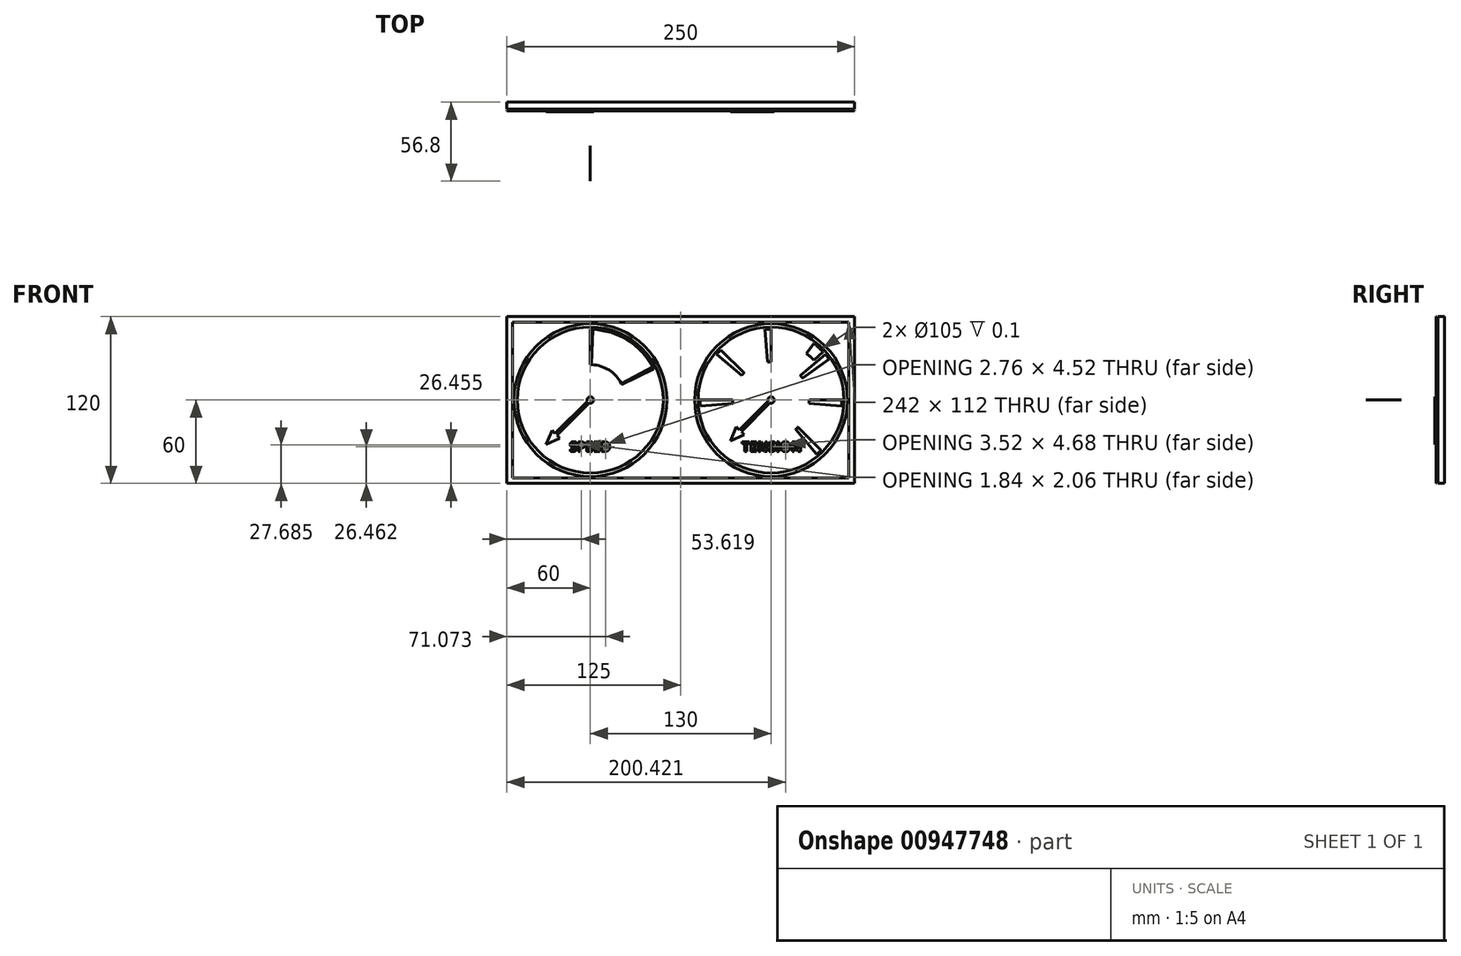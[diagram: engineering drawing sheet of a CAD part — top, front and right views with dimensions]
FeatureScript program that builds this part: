
annotation { "Feature Type Name" : "Feature", "Feature Type Description" : "" }
export const myFeature = defineFeature(function(context is Context, id is Id, definition is map)
    precondition{}
    {
        {
            var Q0;
            Q0=qCreatedBy(makeId("Right.planeOp"),FACE);
            var sketch = newSketch(context, id + "F0", { "sketchPlane" : qUnion([Q0])});
            skLineSegment(sketch, "E0", {"start": v(0, 0) * mm, "end": v(-116.06, 0) * mm, "construction": true});
            skSolve(sketch);
        }
        {
            var Q0;
            Q0=qCreatedBy(makeId("Right.planeOp"),FACE);
            var Q1;
            Q1=sQuery(id+"F0.wireOp",EDGE,"E0");
            cPlane(context, id + "F1", {"entities" : qUnion([Q0, Q1]), "cplaneType" : CPlaneType.LINE_ANGLE, "offset" : 25 * mm, "angle" : 135 * degree, "width" : 150 * mm, "height" : 150 * mm});
        }
        {
            var Q0;
            Q0=qCreatedBy(id+"F1.planeOp",FACE);
            var sketch = newSketch(context, id + "F2", { "sketchPlane" : qUnion([Q0])});
            skLineSegment(sketch, "E1.bottom", {"start": v(-25.4, 0) * mm, "end": v(-50.8, 0) * mm});
            skLineSegment(sketch, "E1.top", {"start": v(-25.4, 0) * mm, "end": v(-50.8, 0) * mm});
            skLineSegment(sketch, "E1.left", {"start": v(-25.4, 0) * mm, "end": v(-25.4, 0) * mm});
            skLineSegment(sketch, "E1.right", {"start": v(-50.8, 0) * mm, "end": v(-50.8, 0) * mm});
            skSolve(sketch);
        }
        {
            var Q0;
            Q0=qSketchRegion(id+"F2",true);
            var Q1;
            Q1=sQuery(id+"F0.wireOp",EDGE,"E0");
            revolve(context, id + "F3", {"surfaceOperationType" : NewSurfaceOperationType.NEW, "entities" : qUnion([Q0]), "axis" : qUnion([Q1]), "revolveType" : RevolveType.ONE_DIRECTION, "oppositeDirection" : true, "angle" : 135 * degree});
        }
        {
            var Q0;
            Q0=qCreatedBy(makeId("Right.planeOp"),FACE);
            var sketch = newSketch(context, id + "F4", { "sketchPlane" : qUnion([Q0])});
            skLineSegment(sketch, "E2.bottom", {"start": v(-0.01, 50.8) * mm, "end": v(0, 50.8) * mm});
            skLineSegment(sketch, "E2.top", {"start": v(0, 25.4) * mm, "end": v(0, 25.4) * mm});
            skLineSegment(sketch, "E2.left", {"start": v(-0.01, 50.8) * mm, "end": v(0, 25.4) * mm});
            skLineSegment(sketch, "E2.right", {"start": v(0, 50.8) * mm, "end": v(0, 25.4) * mm});
            skSolve(sketch);
        }
        {
            var Q0;
            Q0=qSketchRegion(id+"F4",true);
            var Q1;
            Q1=sQuery(id+"F0.wireOp",EDGE,"E0");
            revolve(context, id + "F5", {"surfaceOperationType" : NewSurfaceOperationType.NEW, "entities" : qUnion([Q0]), "axis" : qUnion([Q1]), "revolveType" : RevolveType.ONE_DIRECTION, "oppositeDirection" : true, "angle" : 2 * degree});
        }
        {
            var Q0;
            Q0=qCreatedBy(makeId("Right.planeOp"),FACE);
            var Q1;
            Q1=sQuery(id+"F0.wireOp",EDGE,"E0");
            cPlane(context, id + "F6", {"entities" : qUnion([Q0, Q1]), "cplaneType" : CPlaneType.LINE_ANGLE, "offset" : 25 * mm, "angle" : 2 * degree, "oppositeDirection" : true, "width" : 150 * mm, "height" : 150 * mm});
        }
        {
            var Q0;
            Q0=qCreatedBy(id+"F6.planeOp",FACE);
            var sketch = newSketch(context, id + "F7", { "sketchPlane" : qUnion([Q0])});
            skLineSegment(sketch, "E3.bottom", {"start": v(0, 50.8) * mm, "end": v(0, 50.8) * mm});
            skLineSegment(sketch, "E3.top", {"start": v(0, 25.4) * mm, "end": v(0, 25.4) * mm});
            skLineSegment(sketch, "E3.left", {"start": v(0, 50.8) * mm, "end": v(0, 25.4) * mm});
            skLineSegment(sketch, "E3.right", {"start": v(0, 50.8) * mm, "end": v(0, 25.4) * mm});
            skSolve(sketch);
        }
        {
            var Q0;
            Q0=qSketchRegion(id+"F7",true);
            var Q1;
            Q1=sQuery(id+"F0.wireOp",EDGE,"E0");
            revolve(context, id + "F8", {"surfaceOperationType" : NewSurfaceOperationType.NEW, "entities" : qUnion([Q0]), "axis" : qUnion([Q1]), "revolveType" : RevolveType.ONE_DIRECTION, "oppositeDirection" : true, "angle" : 60 * degree});
        }
        {
            var Q0;
            Q0=qCreatedBy(id+"F6.planeOp",FACE);
            var Q1;
            Q1=sQuery(id+"F0.wireOp",EDGE,"E0");
            cPlane(context, id + "F9", {"entities" : qUnion([Q0, Q1]), "cplaneType" : CPlaneType.LINE_ANGLE, "offset" : 25 * mm, "angle" : 60 * degree, "oppositeDirection" : true, "width" : 150 * mm, "height" : 150 * mm});
        }
        {
            var Q0;
            Q0=qCreatedBy(id+"F9.planeOp",FACE);
            var sketch = newSketch(context, id + "F10", { "sketchPlane" : qUnion([Q0])});
            skLineSegment(sketch, "E4.bottom", {"start": v(50.8, 0) * mm, "end": v(25.4, 0) * mm});
            skLineSegment(sketch, "E4.top", {"start": v(50.8, 0) * mm, "end": v(25.4, -0.01) * mm});
            skLineSegment(sketch, "E4.left", {"start": v(50.8, 0) * mm, "end": v(50.8, 0) * mm});
            skLineSegment(sketch, "E4.right", {"start": v(25.4, 0) * mm, "end": v(25.4, -0.01) * mm});
            skSolve(sketch);
        }
        {
            var Q0;
            Q0=qSketchRegion(id+"F10",true);
            var Q1;
            Q1=sQuery(id+"F0.wireOp",EDGE,"E0");
            revolve(context, id + "F11", {"surfaceOperationType" : NewSurfaceOperationType.NEW, "entities" : qUnion([Q0]), "axis" : qUnion([Q1]), "revolveType" : RevolveType.ONE_DIRECTION, "oppositeDirection" : true, "angle" : 2 * degree});
        }
        {
            var Q0;
            Q0=qCreatedBy(makeId("Front.planeOp"),FACE);
            var sketch = newSketch(context, id + "F12", { "sketchPlane" : qUnion([Q0])});
            skLineSegment(sketch, "E5.bottom", {"start": v(-0.77, -2.19) * mm, "end": v(-24.04, -25.46) * mm});
            skLineSegment(sketch, "E5.top", {"start": v(-2.19, -0.77) * mm, "end": v(-25.46, -24.04) * mm});
            skPoint(sketch, "E5.middle", {"position": v(0, 0) * mm});
            skLineSegment(sketch, "E6", {"start": v(0, 0) * mm, "end": v(0, 10.99) * mm, "construction": true});
            skPoint(sketch, "E7", {"position": v(-24.75, -24.75) * mm});
            skCircle(sketch, "E8", {"center": v(-24.75, -24.75) * mm, "radius": 10.19 * mm, "construction": true});
            skLineSegment(sketch, "E9", {"start": v(-24.04, -25.46) * mm, "end": v(-21.92, -27.58) * mm});
            skLineSegment(sketch, "E10", {"start": v(-25.46, -24.04) * mm, "end": v(-27.58, -21.92) * mm});
            skLineSegment(sketch, "E11", {"start": v(-24.75, -24.75) * mm, "end": v(-31.95, -31.95) * mm, "construction": true});
            skLineSegment(sketch, "E12", {"start": v(-31.95, -31.95) * mm, "end": v(-27.58, -21.92) * mm});
            skLineSegment(sketch, "E13", {"start": v(-21.92, -27.58) * mm, "end": v(-31.95, -31.95) * mm});
            skArc(sketch, "E14", {"start": v(-0.77, -2.19) * mm, "mid": v(1.64, 1.64) * mm, "end": v(-2.19, -0.77) * mm});
            skPoint(sketch, "E15.orphan", {"position": v(-0.7, 0.7) * mm});
            skPoint(sketch, "E16.end.orphan", {"position": v(0.7, -0.7) * mm});
            skSolve(sketch);
        }
        {
            var Q0;
            Q0=qSketchRegion(id+"F12",true);
            extrude(context, id + "F13", {"entities" : qUnion([Q0]), "depth" : 1 * mm, "offsetDistance" : 25 * mm});
        }
        {
            var Q0;
            Q0=qCreatedBy(makeId("Front.planeOp"),FACE);
            var sketch = newSketch(context, id + "F14", { "sketchPlane" : qUnion([Q0])});
            skCircle(sketch, "E17", {"center": v(0, 0) * mm, "radius": 52.5 * mm});
            skCircle(sketch, "E18", {"center": v(0, 0) * mm, "radius": 55 * mm});
            skSolve(sketch);
        }
        {
            var Q0;
            Q0=qSketchRegion(id+"F14",true);
            extrude(context, id + "F15", {"entities" : qUnion([Q0]), "depth" : .1 * mm, "offsetDistance" : 25 * mm});
        }
        {
            var Q0;
            Q0=qCreatedBy(makeId("Front.planeOp"),FACE);
            var sketch = newSketch(context, id + "F16", { "sketchPlane" : qUnion([Q0])});
            skCircle(sketch, "E19", {"center": v(130, 0) * mm, "radius": 52.5 * mm});
            skCircle(sketch, "E20", {"center": v(130, 0) * mm, "radius": 55 * mm});
            skSolve(sketch);
        }
        {
            var Q0;
            Q0=qSketchRegion(id+"F16",true);
            extrude(context, id + "F17", {"entities" : qUnion([Q0]), "depth" : .1 * mm, "offsetDistance" : 25 * mm});
        }
        {
            var Q0;
            Q0=qCreatedBy(makeId("Front.planeOp"),FACE);
            var sketch = newSketch(context, id + "F18", { "sketchPlane" : qUnion([Q0])});
            skArc(sketch, "E21", {"start": v(79.2, -4.44) * mm, "mid": v(79.05, -2.22) * mm, "end": v(79, 0) * mm});
            skLineSegment(sketch, "E22", {"start": v(79, 0) * mm, "end": v(102.5, 0) * mm});
            skLineSegment(sketch, "E23", {"start": v(102.6, -2.4) * mm, "end": v(79.2, -4.44) * mm});
            skArc(sketch, "E24", {"start": v(102.5, 0) * mm, "mid": v(102.53, -1.2) * mm, "end": v(102.6, -2.4) * mm});
            skSolve(sketch);
        }
        {
            var Q0;
            Q0=qSketchRegion(id+"F18",true);
            extrude(context, id + "F19", {"entities" : qUnion([Q0]), "depth" : .1 * mm, "offsetDistance" : 25 * mm});
        }
        {
            var Q0;
            Q0=qCreatedBy(makeId("Front.planeOp"),FACE);
            var sketch = newSketch(context, id + "F20", { "sketchPlane" : qUnion([Q0])});
            skLineSegment(sketch, "E25", {"start": v(130, 0) * mm, "end": v(223.12, 0) * mm, "construction": true});
            skLineSegment(sketch, "E26", {"start": v(147.68, -21.07) * mm, "end": v(162.78, -39.07) * mm});
            skArc(sketch, "E27", {"start": v(147.68, -21.07) * mm, "mid": v(148.58, -20.28) * mm, "end": v(149.45, -19.45) * mm});
            skArc(sketch, "E28", {"start": v(162.78, -39.07) * mm, "mid": v(164.46, -37.6) * mm, "end": v(166.06, -36.06) * mm});
            skLineSegment(sketch, "E29", {"start": v(149.45, -19.45) * mm, "end": v(166.06, -36.06) * mm});
            skSolve(sketch);
        }
        {
            var Q0;
            Q0=qSketchRegion(id+"F20",true);
            extrude(context, id + "F21", {"entities" : qUnion([Q0]), "depth" : .1 * mm, "offsetDistance" : 25 * mm});
        }
        {
            var Q0;
            Q0=qCreatedBy(makeId("Front.planeOp"),FACE);
            var sketch = newSketch(context, id + "F22", { "sketchPlane" : qUnion([Q0])});
            skLineSegment(sketch, "E30", {"start": v(130, 27.5) * mm, "end": v(130, 51) * mm});
            skLineSegment(sketch, "E31", {"start": v(127.6, 27.4) * mm, "end": v(125.56, 50.8) * mm});
            skArc(sketch, "E32", {"start": v(127.6, 27.4) * mm, "mid": v(128.8, 27.47) * mm, "end": v(130, 27.5) * mm});
            skArc(sketch, "E33", {"start": v(125.56, 50.8) * mm, "mid": v(127.78, 50.95) * mm, "end": v(130, 51) * mm});
            skSolve(sketch);
        }
        {
            var Q0;
            Q0=qSketchRegion(id+"F22",true);
            extrude(context, id + "F23", {"entities" : qUnion([Q0]), "depth" : .1 * mm, "offsetDistance" : 25 * mm});
        }
        {
            var Q0;
            Q0=qCreatedBy(makeId("Front.planeOp"),FACE);
            var sketch = newSketch(context, id + "F24", { "sketchPlane" : qUnion([Q0])});
            skLineSegment(sketch, "E34", {"start": v(110.55, 19.45) * mm, "end": v(93.94, 36.06) * mm});
            skLineSegment(sketch, "E35", {"start": v(130, 0) * mm, "end": v(130, 16.9) * mm, "construction": true});
            skLineSegment(sketch, "E36", {"start": v(108.93, 17.68) * mm, "end": v(90.93, 32.78) * mm});
            skArc(sketch, "E37", {"start": v(93.94, 36.06) * mm, "mid": v(92.4, 34.46) * mm, "end": v(90.93, 32.78) * mm});
            skArc(sketch, "E38", {"start": v(110.55, 19.45) * mm, "mid": v(109.72, 18.58) * mm, "end": v(108.93, 17.68) * mm});
            skSolve(sketch);
        }
        {
            var Q0;
            Q0=qSketchRegion(id+"F24",true);
            extrude(context, id + "F25", {"entities" : qUnion([Q0]), "depth" : .1 * mm, "offsetDistance" : 25 * mm});
        }
        {
            var Q0;
            Q0=qCreatedBy(makeId("Front.planeOp"),FACE);
            var sketch = newSketch(context, id + "F26", { "sketchPlane" : qUnion([Q0])});
            skLineSegment(sketch, "E39", {"start": v(151.07, 17.68) * mm, "end": v(169.07, 32.78) * mm});
            skLineSegment(sketch, "E40", {"start": v(130, 0) * mm, "end": v(130, 13.97) * mm, "construction": true});
            skLineSegment(sketch, "E41", {"start": v(152.53, 15.77) * mm, "end": v(171.78, 29.25) * mm});
            skArc(sketch, "E42", {"start": v(151.07, 17.68) * mm, "mid": v(151.82, 16.74) * mm, "end": v(152.53, 15.77) * mm});
            skArc(sketch, "E43", {"start": v(169.07, 32.78) * mm, "mid": v(170.46, 31.05) * mm, "end": v(171.78, 29.25) * mm});
            skSolve(sketch);
        }
        {
            var Q0;
            Q0=qSketchRegion(id+"F26",true);
            extrude(context, id + "F27", {"entities" : qUnion([Q0]), "depth" : .1 * mm, "offsetDistance" : 25 * mm});
        }
        {
            var Q0;
            Q0=qCreatedBy(makeId("Front.planeOp"),FACE);
            var sketch = newSketch(context, id + "F28", { "sketchPlane" : qUnion([Q0])});
            skLineSegment(sketch, "E44", {"start": v(157.5, 0) * mm, "end": v(181, 0) * mm});
            skLineSegment(sketch, "E45", {"start": v(157.4, -2.4) * mm, "end": v(180.8, -4.44) * mm});
            skArc(sketch, "E46", {"start": v(181, 0) * mm, "mid": v(180.95, -2.22) * mm, "end": v(180.8, -4.44) * mm});
            skArc(sketch, "E47", {"start": v(157.5, 0) * mm, "mid": v(157.47, -1.2) * mm, "end": v(157.4, -2.4) * mm});
            skSolve(sketch);
        }
        {
            var Q0;
            Q0=qSketchRegion(id+"F28",true);
            extrude(context, id + "F29", {"entities" : qUnion([Q0]), "depth" : .1 * mm, "offsetDistance" : 25 * mm});
        }
        {
            var Q0;
            Q0=qCreatedBy(makeId("Front.planeOp"),FACE);
            var sketch = newSketch(context, id + "F30", { "sketchPlane" : qUnion([Q0])});
            skLineSegment(sketch, "E48", {"start": v(160.77, 28.58) * mm, "end": v(167.37, 34.7) * mm});
            skLineSegment(sketch, "E49", {"start": v(155.34, 33.5) * mm, "end": v(160.77, 40.67) * mm});
            skArc(sketch, "E50", {"start": v(167.37, 34.7) * mm, "mid": v(164.2, 37.83) * mm, "end": v(160.77, 40.67) * mm});
            skArc(sketch, "E51", {"start": v(160.77, 28.58) * mm, "mid": v(158.17, 31.16) * mm, "end": v(155.34, 33.5) * mm});
            skSolve(sketch);
        }
        {
            var Q0;
            Q0=qSketchRegion(id+"F30",true);
            extrude(context, id + "F31", {"entities" : qUnion([Q0]), "depth" : .1 * mm, "offsetDistance" : 25 * mm});
        }
        {
            var Q0;
            Q0=qCreatedBy(makeId("Front.planeOp"),FACE);
            var sketch = newSketch(context, id + "F32", { "sketchPlane" : qUnion([Q0])});
            skLineSegment(sketch, "E52.bottom", {"start": v(129.23, -2.19) * mm, "end": v(108.62, -22.8) * mm});
            skLineSegment(sketch, "E52.top", {"start": v(127.81, -0.77) * mm, "end": v(107.2, -21.38) * mm});
            skPoint(sketch, "E52.middle", {"position": v(130, 0) * mm});
            skLineSegment(sketch, "E53", {"start": v(130, 0) * mm, "end": v(130, 10.99) * mm, "construction": true});
            skPoint(sketch, "E54", {"position": v(107.9, -22.1) * mm});
            skCircle(sketch, "E55", {"center": v(107.9, -22.1) * mm, "radius": 10.19 * mm, "construction": true});
            skLineSegment(sketch, "E56", {"start": v(108.62, -22.8) * mm, "end": v(110.74, -24.92) * mm});
            skLineSegment(sketch, "E57", {"start": v(107.2, -21.38) * mm, "end": v(105.08, -19.26) * mm});
            skLineSegment(sketch, "E58", {"start": v(107.9, -22.1) * mm, "end": v(100.7, -29.3) * mm, "construction": true});
            skLineSegment(sketch, "E59", {"start": v(100.7, -29.3) * mm, "end": v(105.08, -19.26) * mm});
            skLineSegment(sketch, "E60", {"start": v(110.74, -24.92) * mm, "end": v(100.7, -29.3) * mm});
            skArc(sketch, "E61", {"start": v(129.23, -2.19) * mm, "mid": v(131.64, 1.64) * mm, "end": v(127.81, -0.77) * mm});
            skPoint(sketch, "E62.orphan", {"position": v(129.3, 0.7) * mm});
            skPoint(sketch, "E63.end.orphan", {"position": v(130.7, -0.7) * mm});
            skSolve(sketch);
        }
        {
            var Q0;
            Q0=qSketchRegion(id+"F32",true);
            extrude(context, id + "F33", {"entities" : qUnion([Q0]), "depth" : 1 * mm, "offsetDistance" : 25 * mm});
        }
        {
            var Q0;
            Q0=qCreatedBy(makeId("Front.planeOp"),FACE);
            var sketch = newSketch(context, id + "F34", { "sketchPlane" : qUnion([Q0])});
            skLineSegment(sketch, "E64", {"start": v(0, 0) * mm, "end": v(130, 0) * mm, "construction": true});
            skLineSegment(sketch, "E65.bottom", {"start": v(186, -56) * mm, "end": v(-56, -56) * mm});
            skLineSegment(sketch, "E65.top", {"start": v(186, 56) * mm, "end": v(-56, 56) * mm});
            skLineSegment(sketch, "E65.left", {"start": v(186, -56) * mm, "end": v(186, 56) * mm});
            skLineSegment(sketch, "E65.right", {"start": v(-56, -56) * mm, "end": v(-56, 56) * mm});
            skPoint(sketch, "E65.middle", {"position": v(65, 0) * mm});
            skLineSegment(sketch, "E66.bottom", {"start": v(190, -60) * mm, "end": v(-60, -60) * mm});
            skLineSegment(sketch, "E66.top", {"start": v(190, 60) * mm, "end": v(-60, 60) * mm});
            skLineSegment(sketch, "E66.left", {"start": v(190, -60) * mm, "end": v(190, 60) * mm});
            skLineSegment(sketch, "E66.right", {"start": v(-60, -60) * mm, "end": v(-60, 60) * mm});
            skText(sketch, "E67", { "text": "SPEED", "fontName": "OpenSans-Bold.ttf"});
            skText(sketch, "E68", { "text": "TENSION", "fontName": "OpenSans-Regular.ttf"});
            skLineSegment(sketch, "E69", {"start": v(-15.3, -30.02) * mm, "end": v(165.4, -30.02) * mm, "construction": true});
            const initialGuessF34  = {"E67": [-0.0153, -0.03702, 1, 0, 0.007], "E68": [0.10955, -0.03702, 1, 0, 0.007]};
            skSetInitialGuess(sketch, initialGuessF34);
            skSolve(sketch);
        }
        {
            var Q0;
            Q0=qSketchRegion(id+"F34",true);
            extrude(context, id + "F35", {"entities" : qUnion([Q0]), "depth" : .1 * mm, "offsetDistance" : 25 * mm});
        }
        {
            var Q0;
            Q0=qCreatedBy(makeId("Front.planeOp"),FACE);
            var sketch = newSketch(context, id + "F36", { "sketchPlane" : qUnion([Q0])});
            skLineSegment(sketch, "E70", {"start": v(3.26, -76.77) * mm, "end": v(133.26, -76.77) * mm, "construction": true});
            skPoint(sketch, "E71.middle", {"position": v(68.26, -76.77) * mm});
            skText(sketch, "E72", { "text": "SPEED", "fontName": "OpenSans-Bold.ttf"});
            skText(sketch, "E73", { "text": "TENSION", "fontName": "OpenSans-Bold.ttf"});
            skLineSegment(sketch, "E74", {"start": v(-15, -30.02) * mm, "end": v(168.67, -30.02) * mm, "construction": true});
            skPoint(sketch, "E75", {"position": v(76.84, -30.02) * mm});
            skLineSegment(sketch, "E76", {"start": v(0, 0) * mm, "end": v(0, -24.7) * mm, "construction": true});
            const initialGuessF36  = {"E72": [-0.015, -0.03702, 1, 0, 0.007], "E73": [0.109, -0.03702, 1, 0, 0.007]};
            skSetInitialGuess(sketch, initialGuessF36);
            skSolve(sketch);
        }
        {
            var Q0;
            Q0=qSketchRegion(id+"F36",true);
            extrude(context, id + "F37", {"entities" : qUnion([Q0]), "depth" : .1 * mm, "offsetDistance" : 25 * mm});
        }
        {
            var Q0;
            Q0=qCreatedBy(makeId("Front.planeOp"),FACE);
            var sketch = newSketch(context, id + "F38", { "sketchPlane" : qUnion([Q0])});
            skLineSegment(sketch, "E77.bottom", {"start": v(-60, 60) * mm, "end": v(190, 60) * mm});
            skLineSegment(sketch, "E77.top", {"start": v(-60, -60) * mm, "end": v(190, -60) * mm});
            skLineSegment(sketch, "E77.left", {"start": v(-60, 60) * mm, "end": v(-60, -60) * mm});
            skLineSegment(sketch, "E77.right", {"start": v(190, 60) * mm, "end": v(190, -60) * mm});
            skSolve(sketch);
        }
        {
            var Q0;
            Q0 = qSketchRegion(id + "F38", true);
            extrude(context, id + "F39", {"entities" : qUnion([Q0]), "oppositeDirection" : true, "depth" : 5 * mm, "offsetDistance" : 25 * mm});
        }
        {
            var Q0;
            Q0=makeQuery(id+"F39.opExtrude","SWEPT_BODY",BODY,{"disambiguationData":[OSD([sQuery(id+"F38.wireOp",EDGE,"E77.bottom"),sQuery(id+"F38.wireOp",EDGE,"E77.top"),sQuery(id+"F38.wireOp",EDGE,"E77.left"),sQuery(id+"F38.wireOp",EDGE,"E77.right")])]});
            transform(context, id + "F40", {"entities" : qUnion([Q0]), "transformType" : TransformType.TRANSLATION_3D, "dx" : 0 * mm, "dy" : 1 * mm, "dz" : 0 * mm, "makeCopy" : false});
        }
    });
